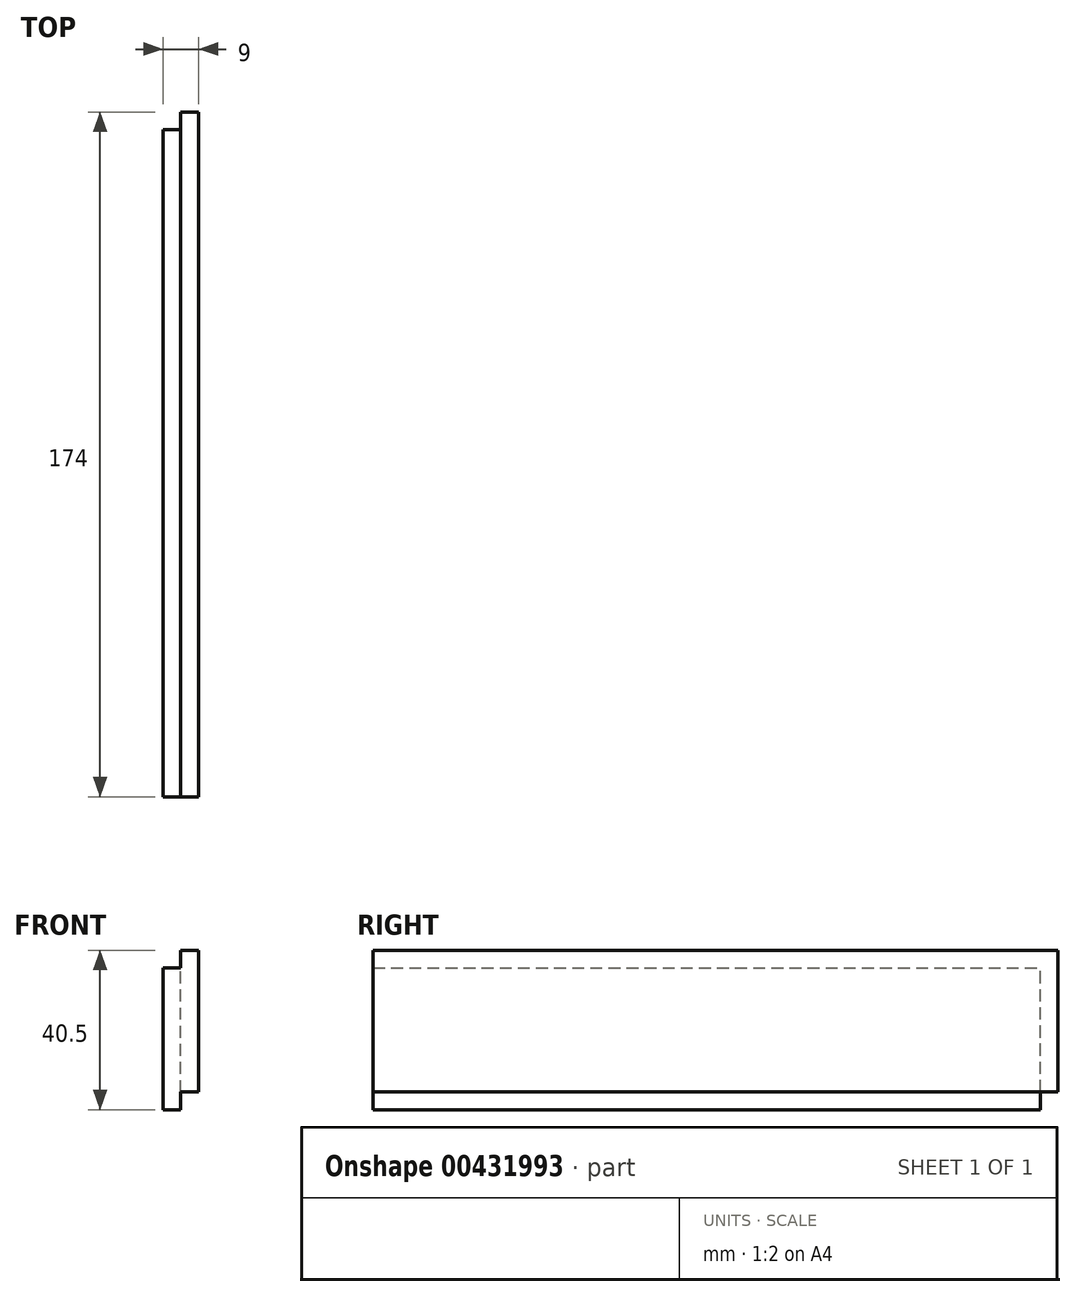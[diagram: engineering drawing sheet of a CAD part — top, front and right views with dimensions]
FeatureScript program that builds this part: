
annotation { "Feature Type Name" : "Feature", "Feature Type Description" : "" }
export const myFeature = defineFeature(function(context is Context, id is Id, definition is map)
    precondition{}
    {
        {
            var Q0;
            Q0=qCreatedBy(makeId("Right.planeOp"),FACE);
            var sketch = newSketch(context, id + "F0", { "sketchPlane" : qUnion([Q0])});
            skLineSegment(sketch, "E0.bottom", {"start": v(-87, 20.25) * mm, "end": v(87, 20.25) * mm});
            skLineSegment(sketch, "E0.top", {"start": v(-87, -20.25) * mm, "end": v(87, -20.25) * mm});
            skLineSegment(sketch, "E0.left", {"start": v(-87, 20.25) * mm, "end": v(-87, -20.25) * mm});
            skLineSegment(sketch, "E0.right", {"start": v(87, 20.25) * mm, "end": v(87, -20.25) * mm});
            skPoint(sketch, "E0.middle", {"position": v(0, 0) * mm});
            skSolve(sketch);
        }
        {
            var Q0;
            Q0=qSketchRegion(id+"F0",true);
            extrude(context, id + "F1", {"entities" : qUnion([Q0]), "depth" : 9 * mm, "offsetDistance" : 25 * mm});
        }
        {
            var Q0;
            Q0=makeQuery(id+"F1.opExtrude","SWEPT_FACE",FACE,{"disambiguationData":[OSD([sQuery(id+"F0.wireOp",EDGE,"E0.bottom")])]});
            var sketch = newSketch(context, id + "F2", { "sketchPlane" : qUnion([Q0])});
            skLineSegment(sketch, "E1.bottom", {"start": v(0, 87) * mm, "end": v(4.5, 87) * mm});
            skLineSegment(sketch, "E1.top", {"start": v(0, -87) * mm, "end": v(4.5, -87) * mm});
            skLineSegment(sketch, "E1.left", {"start": v(0, 87) * mm, "end": v(0, -87) * mm});
            skLineSegment(sketch, "E1.right", {"start": v(4.5, 87) * mm, "end": v(4.5, -87) * mm});
            skSolve(sketch);
        }
        {
            var Q0;
            Q0=qSketchRegion(id+"F2",true);
            extrude(context, id + "F3", {"entities" : qUnion([Q0]), "operationType" : NewBodyOperationType.REMOVE, "oppositeDirection" : true, "depth" : 4.5 * mm, "offsetDistance" : 25 * mm});
        }
        {
            var Q0;
            Q0=makeQuery(id+"F3.boolean.opBoolean","COPY",FACE,{"derivedFrom":makeQuery(id+"F3.opExtrude","CAP_FACE",FACE,{"disambiguationData":[OSD([sQuery(id+"F2.wireOp",EDGE,"E1.bottom"),sQuery(id+"F2.wireOp",EDGE,"E1.top"),sQuery(id+"F2.wireOp",EDGE,"E1.left"),sQuery(id+"F2.wireOp",EDGE,"E1.right")])],"isStart":false})});
            var sketch = newSketch(context, id + "F4", { "sketchPlane" : qUnion([Q0])});
            skLineSegment(sketch, "E2.bottom", {"start": v(0, 82.5) * mm, "end": v(4.5, 82.5) * mm});
            skLineSegment(sketch, "E2.top", {"start": v(0, 87) * mm, "end": v(4.5, 87) * mm});
            skLineSegment(sketch, "E2.left", {"start": v(0, 82.5) * mm, "end": v(0, 87) * mm});
            skLineSegment(sketch, "E2.right", {"start": v(4.5, 82.5) * mm, "end": v(4.5, 87) * mm});
            skSolve(sketch);
        }
        {
            var Q0;
            Q0=qSketchRegion(id+"F4",true);
            extrude(context, id + "F5", {"entities" : qUnion([Q0]), "operationType" : NewBodyOperationType.REMOVE, "endBound" : BoundingType.UP_TO_NEXT, "oppositeDirection" : true, "depth" : 6 * mm});
        }
        {
            var Q0;
            Q0=makeQuery(id+"F1.opExtrude","SWEPT_FACE",FACE,{"disambiguationData":[OSD([sQuery(id+"F0.wireOp",EDGE,"E0.top")])]});
            var sketch = newSketch(context, id + "F6", { "sketchPlane" : qUnion([Q0])});
            skLineSegment(sketch, "E3.bottom", {"start": v(9, 87) * mm, "end": v(4.5, 87) * mm});
            skLineSegment(sketch, "E3.top", {"start": v(9, -87) * mm, "end": v(4.5, -87) * mm});
            skLineSegment(sketch, "E3.left", {"start": v(9, 87) * mm, "end": v(9, -87) * mm});
            skLineSegment(sketch, "E3.right", {"start": v(4.5, 87) * mm, "end": v(4.5, -87) * mm});
            skSolve(sketch);
        }
        {
            var Q0;
            Q0=qSketchRegion(id+"F6",true);
            extrude(context, id + "F7", {"entities" : qUnion([Q0]), "operationType" : NewBodyOperationType.REMOVE, "oppositeDirection" : true, "depth" : 4.5 * mm, "offsetDistance" : 25 * mm});
        }
    });
